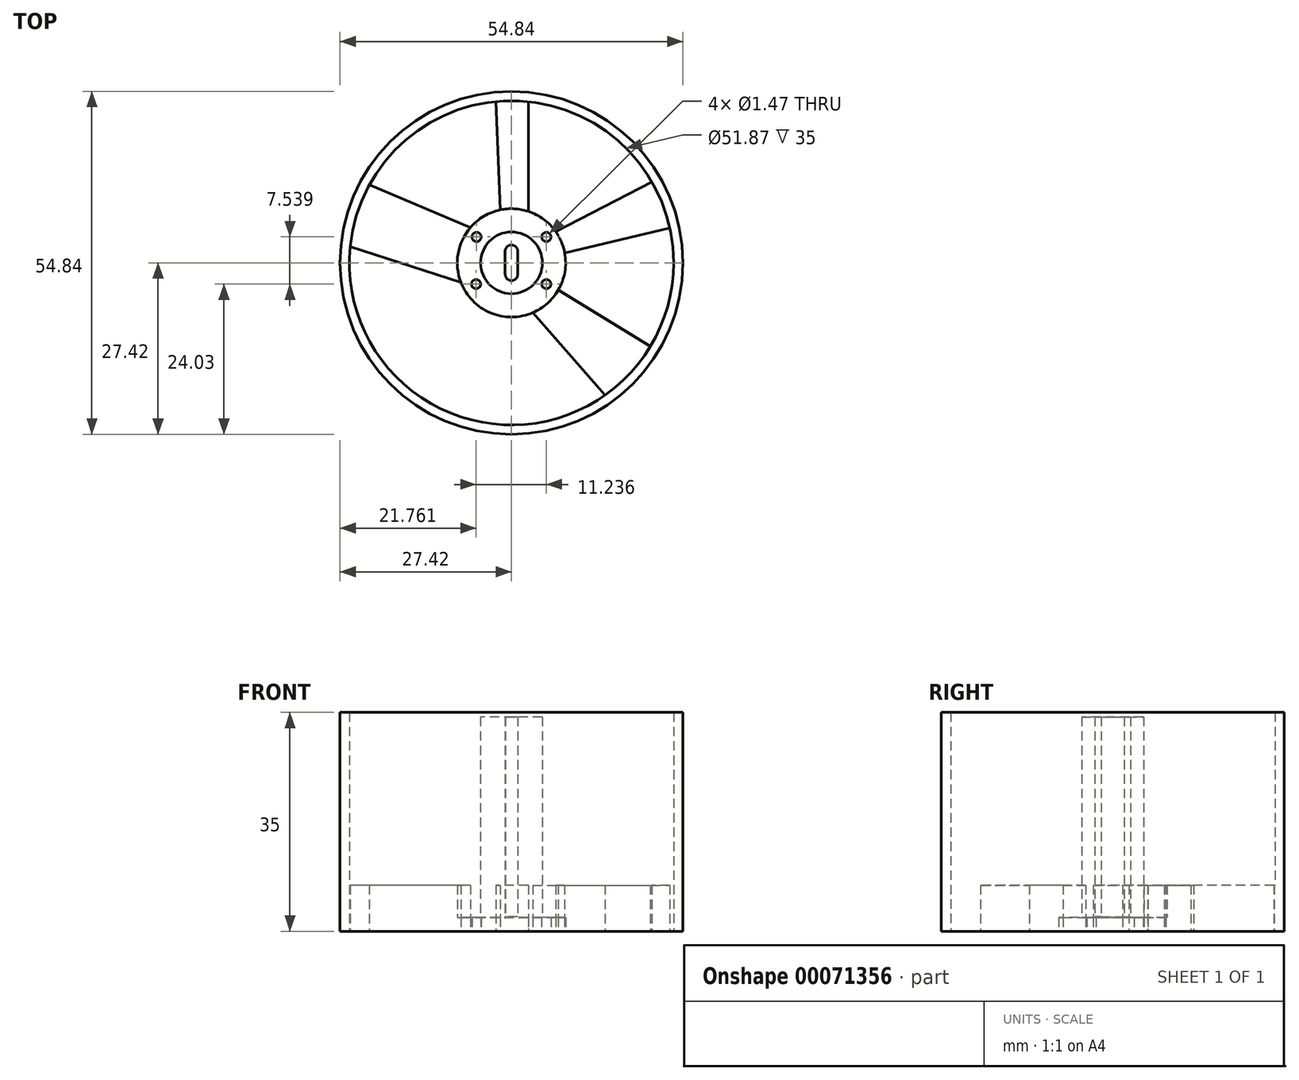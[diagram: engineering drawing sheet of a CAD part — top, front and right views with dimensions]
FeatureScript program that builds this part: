
annotation { "Feature Type Name" : "Feature", "Feature Type Description" : "" }
export const myFeature = defineFeature(function(context is Context, id is Id, definition is map)
    precondition{}
    {
        {
            var Q0;
            Q0=qCreatedBy(makeId("Top.planeOp"),FACE);
            var sketch = newSketch(context, id + "F0", { "sketchPlane" : qUnion([Q0])});
            skCircle(sketch, "E0", {"center": v(0, 0) * mm, "radius": 4.94 * mm});
            skCircle(sketch, "E1", {"center": v(0, 0) * mm, "radius": 8.66 * mm});
            skCircle(sketch, "E2", {"center": v(5.58, -3.4) * mm, "radius": 0.73 * mm});
            skCircle(sketch, "E3", {"center": v(-5.66, -3.4) * mm, "radius": 0.73 * mm});
            skCircle(sketch, "E4", {"center": v(5.58, 4.15) * mm, "radius": 0.73 * mm});
            skCircle(sketch, "E5", {"center": v(-5.59, 4.15) * mm, "radius": 0.73 * mm});
            skCircle(sketch, "E6", {"center": v(0, 0) * mm, "radius": 25.93 * mm});
            skLineSegment(sketch, "E7", {"start": v(-6.57, 5.65) * mm, "end": v(-22.73, 12.49) * mm});
            skLineSegment(sketch, "E8", {"start": v(-8.07, -3.15) * mm, "end": v(-25.8, 2.58) * mm});
            skLineSegment(sketch, "E9", {"start": v(-5.76, -6.48) * mm, "end": v(-18.89, -17.78) * mm});
            skLineSegment(sketch, "E10", {"start": v(-18.89, -17.78) * mm, "end": v(-5.76, -6.48) * mm});
            skLineSegment(sketch, "E11", {"start": v(-3.39, -7.98) * mm, "end": v(-11.2, -23.4) * mm});
            skLineSegment(sketch, "E12", {"start": v(3.43, -7.96) * mm, "end": v(14.98, -21.17) * mm});
            skLineSegment(sketch, "E13", {"start": v(7.5, -4.35) * mm, "end": v(22.23, -13.37) * mm});
            skLineSegment(sketch, "E14", {"start": v(8.51, 1.6) * mm, "end": v(25.33, 5.55) * mm});
            skLineSegment(sketch, "E15", {"start": v(7.07, 5.01) * mm, "end": v(22.5, 12.91) * mm});
            skLineSegment(sketch, "E16", {"start": v(-6.15, 25.2) * mm, "end": v(-6.15, 25.2) * mm});
            skLineSegment(sketch, "E17", {"start": v(2.7, 25.8) * mm, "end": v(2.7, 8.23) * mm});
            skLineSegment(sketch, "E18", {"start": v(-2.48, 25.82) * mm, "end": v(-1.8, 8.48) * mm});
            skCircle(sketch, "E19", {"center": v(0, 0) * mm, "radius": 27.42 * mm});
            skSolve(sketch);
        }
        {
            var Q0;
            Q0=makeQuery(id+"F0.imprint","IMPRINT",FACE,{"disambiguationData":[TD([[makeQuery(id+"F0.imprint","IMPRINT",EDGE,{"derivedFrom":sQuery(id+"F0.wireOp",EDGE,"E19")}),1.0]])]});
            extrude(context, id + "F1", {"entities" : qUnion([Q0]), "depth" : 35 * mm});
        }
        {
            var Q0;
            {var subQ0=sQuery(id+"F0.wireOp",EDGE,"E12");Q0=makeQuery(id+"F0.imprint","IMPRINT",FACE,{"disambiguationData":[TD([[makeQuery(id+"F0.imprint","IMPRINT",EDGE,{"derivedFrom":subQ0}),1.0]])]});}
            var Q1;
            {var subQ0=sQuery(id+"F0.wireOp",EDGE,"E14");Q1=makeQuery(id+"F0.imprint","IMPRINT",FACE,{"disambiguationData":[TD([[makeQuery(id+"F0.imprint","IMPRINT",EDGE,{"derivedFrom":subQ0}),1.0]])]});}
            var Q2;
            {var subQ0=sQuery(id+"F0.wireOp",EDGE,"E17");Q2=makeQuery(id+"F0.imprint","IMPRINT",FACE,{"disambiguationData":[TD([[makeQuery(id+"F0.imprint","IMPRINT",EDGE,{"derivedFrom":subQ0}),-1.0]])]});}
            var Q3;
            {var subQ0=sQuery(id+"F0.wireOp",EDGE,"E7");Q3=makeQuery(id+"F0.imprint","IMPRINT",FACE,{"disambiguationData":[TD([[makeQuery(id+"F0.imprint","IMPRINT",EDGE,{"derivedFrom":subQ0}),1.0]])]});}
            var Q4;
            {var subQ0=sQuery(id+"F0.wireOp",EDGE,"E10");Q4=makeQuery(id+"F0.imprint","IMPRINT",FACE,{"disambiguationData":[TD([[makeQuery(id+"F0.imprint","IMPRINT",EDGE,{"derivedFrom":subQ0}),-1.0]])]});}
            extrude(context, id + "F2", {"entities" : qUnion([Q0, Q1, Q2, Q3, Q4]), "operationType" : NewBodyOperationType.ADD, "depth" : 7.35 * mm});
        }
        {
            var Q0;
            Q0=makeQuery(id+"F0.imprint","IMPRINT",FACE,{"disambiguationData":[TD([[makeQuery(id+"F0.imprint","IMPRINT",EDGE,{"derivedFrom":sQuery(id+"F0.wireOp",EDGE,"E0")}),-1.0]])]});
            extrude(context, id + "F3", {"entities" : qUnion([Q0]), "operationType" : NewBodyOperationType.ADD, "depth" : 2.2 * mm});
        }
        {
            var Q0;
            Q0=makeQuery(id+"F0.imprint","IMPRINT",FACE,{"disambiguationData":[TD([[makeQuery(id+"F0.imprint","IMPRINT",EDGE,{"derivedFrom":sQuery(id+"F0.wireOp",EDGE,"E0")}),1.0]])]});
            extrude(context, id + "F4", {"entities" : qUnion([Q0]), "operationType" : NewBodyOperationType.ADD, "depth" : 2.3 * mm});
        }
        {
            var Q0;
            Q0=makeQuery(id+"F4.opExtrude","CAP_FACE",FACE,{"disambiguationData":[OSD([sQuery(id+"F0.wireOp",EDGE,"E0")])],"isStart":false});
            var sketch = newSketch(context, id + "F5", { "sketchPlane" : qUnion([Q0])});
            skLineSegment(sketch, "E20.bottom", {"start": v(1, -1.86) * mm, "end": v(-1, -1.86) * mm});
            skLineSegment(sketch, "E20.top", {"start": v(1, 1.86) * mm, "end": v(-1, 1.86) * mm});
            skLineSegment(sketch, "E20.left", {"start": v(1, -1.86) * mm, "end": v(1, 1.86) * mm});
            skLineSegment(sketch, "E20.right", {"start": v(-1, -1.86) * mm, "end": v(-1, 1.86) * mm});
            skPoint(sketch, "E20.middle", {"position": v(0, 0) * mm});
            skCircle(sketch, "E21", {"center": v(0, 1.86) * mm, "radius": 1 * mm});
            skCircle(sketch, "E22", {"center": v(0, -1.86) * mm, "radius": 0.99 * mm});
            skSolve(sketch);
        }
        {
            var Q0;
            {var subQ4=sQuery(id+"F5.wireOp",EDGE,"E20.left");Q0=makeQuery(id+"F5.imprint","IMPRINT",FACE,{"disambiguationData":[TD([[makeQuery(id+"F5.imprint","IMPRINT",EDGE,{"derivedFrom":subQ4}),-1.0]])]});}
            extrude(context, id + "F6", {"entities" : qUnion([Q0]), "operationType" : NewBodyOperationType.ADD, "depth" : 32 * mm});
        }
    });
